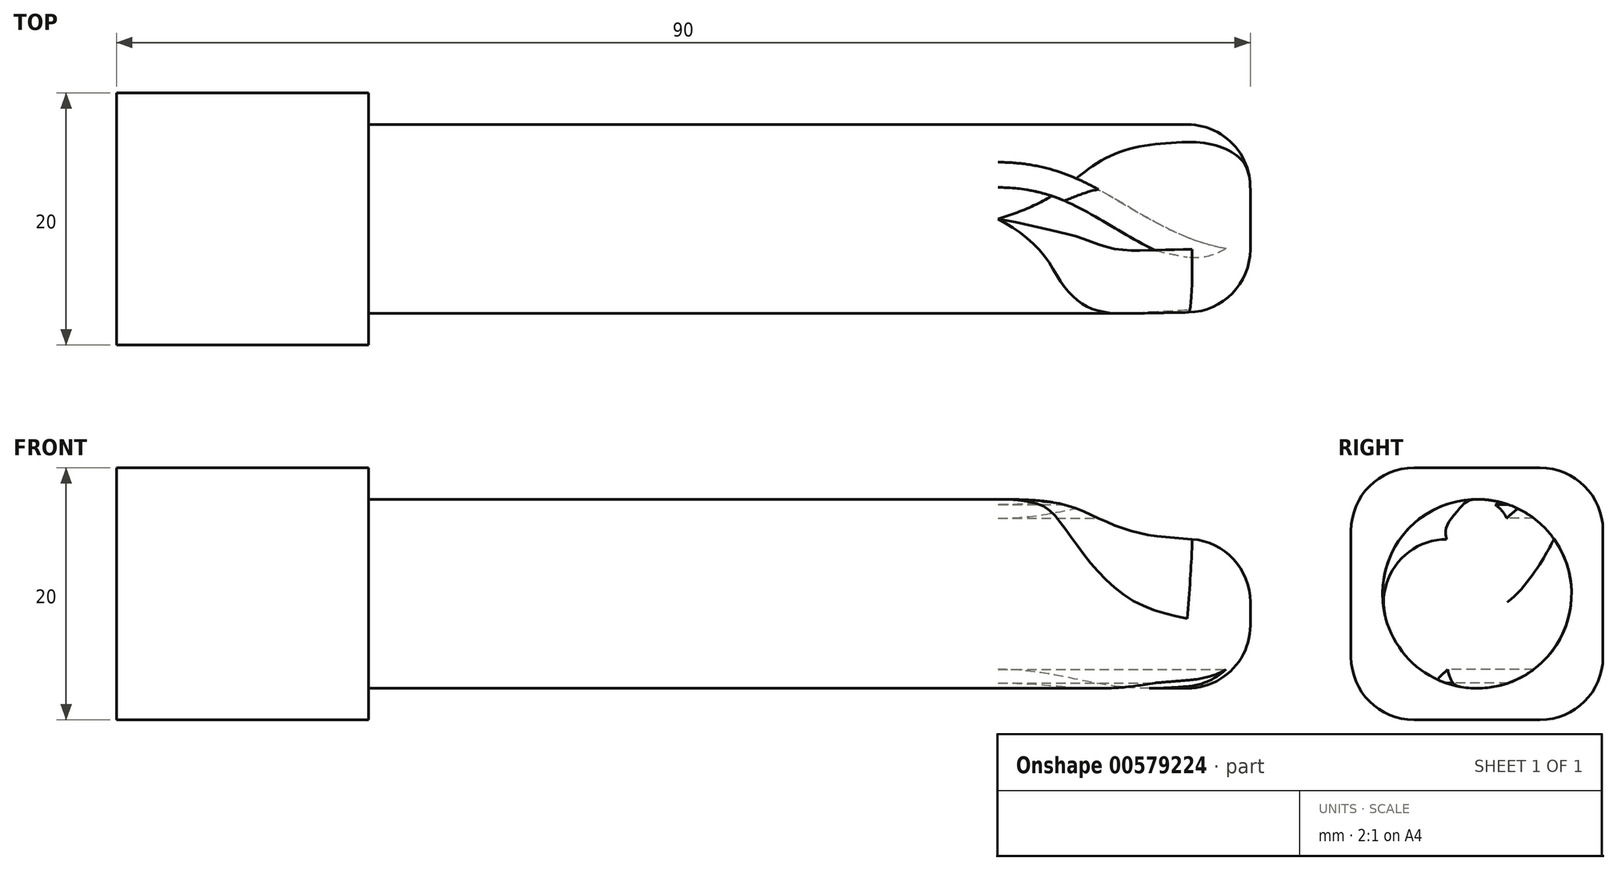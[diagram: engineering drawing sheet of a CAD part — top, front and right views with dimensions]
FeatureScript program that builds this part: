
annotation { "Feature Type Name" : "Feature", "Feature Type Description" : "" }
export const myFeature = defineFeature(function(context is Context, id is Id, definition is map)
    precondition{}
    {
        {
            var Q0;
            Q0=qCreatedBy(makeId("Front.planeOp"),FACE);
            var sketch = newSketch(context, id + "F0", { "sketchPlane" : qUnion([Q0])});
            skLineSegment(sketch, "E0", {"start": v(0, 0) * mm, "end": v(70, 0) * mm});
            skLineSegment(sketch, "E1", {"start": v(70, 0) * mm, "end": v(70, -2.5) * mm});
            skLineSegment(sketch, "E2", {"start": v(65, -7.5) * mm, "end": v(0, -7.5) * mm});
            skLineSegment(sketch, "E3", {"start": v(0, -7.5) * mm, "end": v(0, 0) * mm});
            skPoint(sketch, "E4.visualSharp", {"position": v(70, -7.5) * mm});
            skArc(sketch, "E4.filletArc", {"start": v(65, -7.5) * mm, "mid": v(68.54, -6.04) * mm, "end": v(70, -2.5) * mm});
            skSolve(sketch);
        }
        {
            var Q0;
            Q0=makeQuery(id+"F0.imprint","IMPRINT",FACE,{"disambiguationData":[TD([[makeQuery(id+"F0.imprint","IMPRINT",EDGE,{"derivedFrom":sQuery(id+"F0.wireOp",EDGE,"E0")}),-1.0]])]});
            var Q1;
            Q1=sQuery(id+"F0.wireOp",EDGE,"E0");
            revolve(context, id + "F1", {"entities" : qUnion([Q0]), "axis" : qUnion([Q1]), "revolveType" : RevolveType.FULL});
        }
        {
            var Q0;
            Q0=qCreatedBy(makeId("Front.planeOp"),FACE);
            var sketch = newSketch(context, id + "F2", { "sketchPlane" : qUnion([Q0])});
            skLineSegment(sketch, "E5", {"start": v(-0.02, 7.5) * mm, "end": v(65, 7.5) * mm});
            skPoint(sketch, "E6", {"position": v(49.98, 7.5) * mm});
            skLineSegment(sketch, "E7.0", {"start": v(70, -2.5) * mm, "end": v(70, 2.5) * mm});
            skFitSpline(sketch, "E8", {"points": [v(49.98, 7.5) * mm, v(56.6, 6.6) * mm, v(61.35, 4.79) * mm, v(68.4, 3.94) * mm, v(70, 2.5) * mm], "startDerivative": vector(38.77, 0) * mm, "endDerivative": vector(0, -13.77) * mm});
            skLineSegment(sketch, "E9", {"start": v(49.98, 7.5) * mm, "end": v(70, 7.5) * mm});
            skLineSegment(sketch, "E10", {"start": v(70, 7.5) * mm, "end": v(70, 2.5) * mm});
            skSolve(sketch);
        }
        {
            var Q0;
            {var subQ0=sQuery(id+"F2.wireOp",EDGE,"E8");Q0=makeQuery(id+"F2.imprint","IMPRINT",FACE,{"disambiguationData":[TD([[makeQuery(id+"F2.imprint","IMPRINT",EDGE,{"derivedFrom":subQ0}),1.0]])]});}
            extrude(context, id + "F3", {"entities" : qUnion([Q0]), "operationType" : NewBodyOperationType.REMOVE, "endBound" : BoundingType.SYMMETRIC, "oppositeDirection" : true, "depth" : 25 * mm, "offsetDistance" : 25 * mm});
        }
        {
            var Q0;
            Q0=makeQuery(id+"F3.boolean.opBoolean","INTERSECT",EDGE,{"disambiguationData":[OD(0.0)],"derivedFrom":[makeQuery(id+"F1.opRevolve","SWEPT_FACE",FACE,{"disambiguationData":[OSD([sQuery(id+"F0.wireOp",EDGE,"E2")])]}),makeQuery(id+"F3.opExtrude","SWEPT_FACE",FACE,{"disambiguationData":[OSD([sQuery(id+"F2.wireOp",EDGE,"E8")])]})]});
            fillet(context, id + "F4", {"entities" : qUnion([Q0]), "radius" : 5 * mm, "tangentPropagation" : true, "allowEdgeOverflow" : false});
        }
        {
            var Q0;
            Q0=makeQuery(id+"F1.opRevolve","SWEPT_FACE",FACE,{"disambiguationData":[OSD([sQuery(id+"F0.wireOp",EDGE,"E1")])]});
            var sketch = newSketch(context, id + "F5", { "sketchPlane" : qUnion([Q0])});
            skPoint(sketch, "E11.0", {"position": v(0, 0) * mm});
            skArc(sketch, "E12.0", {"start": v(-7.24, -1.97) * mm, "mid": v(-5.96, 4.55) * mm, "end": v(0, 7.5) * mm});
            skLineSegment(sketch, "E13.bottom", {"start": v(-4.5, 7.5) * mm, "end": v(-2.5, 7.5) * mm});
            skLineSegment(sketch, "E13.top", {"start": v(-4.5, -7.5) * mm, "end": v(-2.5, -7.5) * mm});
            skLineSegment(sketch, "E13.left", {"start": v(-4.5, 7.5) * mm, "end": v(-4.5, -7.5) * mm});
            skLineSegment(sketch, "E13.right", {"start": v(-2.5, 7.5) * mm, "end": v(-2.5, -7.5) * mm});
            skPoint(sketch, "E14.0", {"position": v(0, -7.5) * mm});
            skSolve(sketch);
        }
        {
            var Q0;
            Q0=qCreatedBy(makeId("Right.planeOp"),FACE);
            var Q1;
            {var subQ0=makeQuery(id+"F1.opRevolve","SWEPT_FACE",FACE,{"disambiguationData":[OSD([sQuery(id+"F0.wireOp",EDGE,"E2")])]});var subQ1=makeQuery(id+"F3.opExtrude","SWEPT_FACE",FACE,{"disambiguationData":[OSD([sQuery(id+"F2.wireOp",EDGE,"E8")])]});Q1=makeQuery(id+"F4.opFillet","BLEND_VERTEX",VERTEX,{"blendedFrom":[makeQuery(id+"F3.boolean.opBoolean","INTERSECT",EDGE,{"disambiguationData":[OD(0.0)],"derivedFrom":[subQ0,subQ1]}),makeQuery(id+"F3.boolean.opBoolean","INTERSECT",EDGE,{"disambiguationData":[OD(1.0)],"derivedFrom":[subQ0,subQ1]}),makeQuery(id+"F3.boolean.opBoolean","COPY",FACE,{"derivedFrom":subQ1}),subQ0],"blendedInto":[makeQuery(id+"F3.boolean.opBoolean","COPY",FACE,{"derivedFrom":subQ1}),subQ0]});}
            cPlane(context, id + "F6", {"entities" : qUnion([Q0, Q1]), "cplaneType" : CPlaneType.PLANE_POINT, "offset" : 25 * mm, "width" : 150 * mm, "height" : 150 * mm});
        }
        {
            var Q0;
            Q0=qCreatedBy(id+"F6.planeOp",FACE);
            var sketch = newSketch(context, id + "F7", { "sketchPlane" : qUnion([Q0])});
            skArc(sketch, "E15.0", {"start": v(0, 7.5) * mm, "mid": v(5.96, 4.55) * mm, "end": v(7.24, -1.97) * mm});
            skArc(sketch, "E16.0", {"start": v(7.24, -1.97) * mm, "mid": v(0, -7.5) * mm, "end": v(-7.24, -1.97) * mm});
            skLineSegment(sketch, "E17.0", {"start": v(-4.5, 7.5) * mm, "end": v(-4.5, -7.5) * mm});
            skLineSegment(sketch, "E18.0", {"start": v(-4.5, 7.5) * mm, "end": v(-2.5, 7.5) * mm});
            skLineSegment(sketch, "E19.0", {"start": v(-2.5, 7.5) * mm, "end": v(-2.5, -7.5) * mm});
            skLineSegment(sketch, "E20.0", {"start": v(-4.5, -7.5) * mm, "end": v(-2.5, -7.5) * mm});
            skLineSegment(sketch, "E21", {"start": v(0, 0) * mm, "end": v(0, 10.8) * mm});
            skLineSegment(sketch, "E22.MirrorCS", {"start": v(4.5, 7.5) * mm, "end": v(2.5, 7.5) * mm});
            skLineSegment(sketch, "E23.MirrorCS", {"start": v(4.5, 7.5) * mm, "end": v(4.5, -7.5) * mm});
            skLineSegment(sketch, "E24.MirrorCS", {"start": v(2.5, 7.5) * mm, "end": v(2.5, -7.5) * mm});
            skLineSegment(sketch, "E25.MirrorCS", {"start": v(4.5, -7.5) * mm, "end": v(2.5, -7.5) * mm});
            skSolve(sketch);
        }
        {
            var Q0;
            Q0=qCreatedBy(makeId("Top.planeOp"),FACE);
            var sketch = newSketch(context, id + "F8", { "sketchPlane" : qUnion([Q0])});
            skPoint(sketch, "E26.0", {"position": v(49.98, 2.5) * mm});
            skPoint(sketch, "E27.0", {"position": v(70, -4.5) * mm});
            skPoint(sketch, "E28.0", {"position": v(49.98, 0) * mm});
            skPoint(sketch, "E29.0", {"position": v(70, 0) * mm});
            skLineSegment(sketch, "E30", {"start": v(49.98, 0) * mm, "end": v(70, 0) * mm, "construction": true});
            skPoint(sketch, "E31", {"position": v(60, 0) * mm});
            skLineSegment(sketch, "E32.0", {"start": v(49.98, 4.5) * mm, "end": v(49.98, 2.5) * mm, "construction": true});
            skLineSegment(sketch, "E33.0", {"start": v(70, -4.5) * mm, "end": v(70, -2.5) * mm, "construction": true});
            skPoint(sketch, "E34", {"position": v(49.98, 3.5) * mm});
            skPoint(sketch, "E35", {"position": v(70, -3.5) * mm});
            skFitSpline(sketch, "E36", {"points": [v(49.98, 3.5) * mm, v(55.05, 2.6) * mm, v(60, 0) * mm, v(64.66, -2.4) * mm, v(70, -3.5) * mm], "startDerivative": vector(21.06, 0) * mm, "endDerivative": vector(22.08, 0) * mm});
            skSolve(sketch);
        }
        {
            var Q0;
            {var subQ0=sQuery(id+"F7.wireOp",EDGE,"E24.MirrorCS");var subQ1=sQuery(id+"F7.wireOp",EDGE,"E15.0");var subQ2=makeQuery(id+"F7.imprint","INTERSECT",VERTEX,{"derivedFrom":[subQ1,subQ0]});Q0=makeQuery(id+"F7.imprint","IMPRINT",FACE,{"disambiguationData":[TD([[makeQuery(id+"F7.imprint","IMPRINT",EDGE,{"disambiguationData":[TD([[subQ2,-1.0]])],"derivedFrom":subQ1}),-1.0]])]});}
            var Q1;
            {var subQ5=sQuery(id+"F7.wireOp",EDGE,"E22.MirrorCS");Q1=makeQuery(id+"F7.imprint","IMPRINT",FACE,{"disambiguationData":[TD([[makeQuery(id+"F7.imprint","IMPRINT",EDGE,{"derivedFrom":subQ5}),1.0]])]});}
            var Q2;
            {var subQ5=sQuery(id+"F7.wireOp",EDGE,"E25.MirrorCS");Q2=makeQuery(id+"F7.imprint","IMPRINT",FACE,{"disambiguationData":[TD([[makeQuery(id+"F7.imprint","IMPRINT",EDGE,{"derivedFrom":subQ5}),-1.0]])]});}
            var Q3;
            Q3=sQuery(id+"F8.wireOp",EDGE,"E36");
            sweep(context, id + "F9", {"operationType" : NewBodyOperationType.REMOVE, "profiles" : qUnion([Q0, Q1, Q2]), "path" : qUnion([Q3])});
        }
        {
            var Q0;
            Q0=makeQuery(id+"F1.opRevolve","SWEPT_FACE",FACE,{"disambiguationData":[OSD([sQuery(id+"F0.wireOp",EDGE,"E3")])]});
            var sketch = newSketch(context, id + "F10", { "sketchPlane" : qUnion([Q0])});
            skLineSegment(sketch, "E37.bottom", {"start": v(10, -10) * mm, "end": v(-10, -10) * mm});
            skLineSegment(sketch, "E37.top", {"start": v(10, 10) * mm, "end": v(-10, 10) * mm});
            skLineSegment(sketch, "E37.left", {"start": v(10, -10) * mm, "end": v(10, 10) * mm});
            skLineSegment(sketch, "E37.right", {"start": v(-10, -10) * mm, "end": v(-10, 10) * mm});
            skPoint(sketch, "E37.middle", {"position": v(0, 0) * mm});
            skSolve(sketch);
        }
        {
            var Q0;
            Q0=makeQuery(id+"F10.imprint","IMPRINT",FACE,{"disambiguationData":[TD([[makeQuery(id+"F10.imprint","IMPRINT",EDGE,{"derivedFrom":makeQuery(id+"F1.opRevolve","SWEPT_EDGE",EDGE,{"disambiguationData":[OSD([sQuery(id+"F0.wireOp",EDGE,"E2"),sQuery(id+"F0.wireOp",EDGE,"E3")])]})}),1.0]])]});
            var Q1;
            Q1=makeQuery(id+"F10.imprint","IMPRINT",FACE,{"disambiguationData":[TD([[makeQuery(id+"F10.imprint","IMPRINT",EDGE,{"derivedFrom":sQuery(id+"F10.wireOp",EDGE,"E37.bottom")}),-1.0]])]});
            extrude(context, id + "F11", {"entities" : qUnion([Q0, Q1]), "operationType" : NewBodyOperationType.ADD, "depth" : 20 * mm, "offsetDistance" : 25 * mm});
        }
        {
            var Q0;
            Q0=makeQuery(id+"F11.opExtrude","SWEPT_EDGE",EDGE,{"disambiguationData":[OSD([sQuery(id+"F10.wireOp",EDGE,"E37.top"),sQuery(id+"F10.wireOp",EDGE,"E37.right")])]});
            var Q1;
            Q1=makeQuery(id+"F11.opExtrude","SWEPT_EDGE",EDGE,{"disambiguationData":[OSD([sQuery(id+"F10.wireOp",EDGE,"E37.top"),sQuery(id+"F10.wireOp",EDGE,"E37.left")])]});
            var Q2;
            Q2=makeQuery(id+"F11.opExtrude","SWEPT_EDGE",EDGE,{"disambiguationData":[OSD([sQuery(id+"F10.wireOp",EDGE,"E37.bottom"),sQuery(id+"F10.wireOp",EDGE,"E37.right")])]});
            var Q3;
            Q3=makeQuery(id+"F11.opExtrude","SWEPT_EDGE",EDGE,{"disambiguationData":[OSD([sQuery(id+"F10.wireOp",EDGE,"E37.bottom"),sQuery(id+"F10.wireOp",EDGE,"E37.left")])]});
            fillet(context, id + "F12", {"entities" : qUnion([Q0, Q1, Q2, Q3]), "radius" : 5 * mm, "tangentPropagation" : true, "allowEdgeOverflow" : false});
        }
    });
